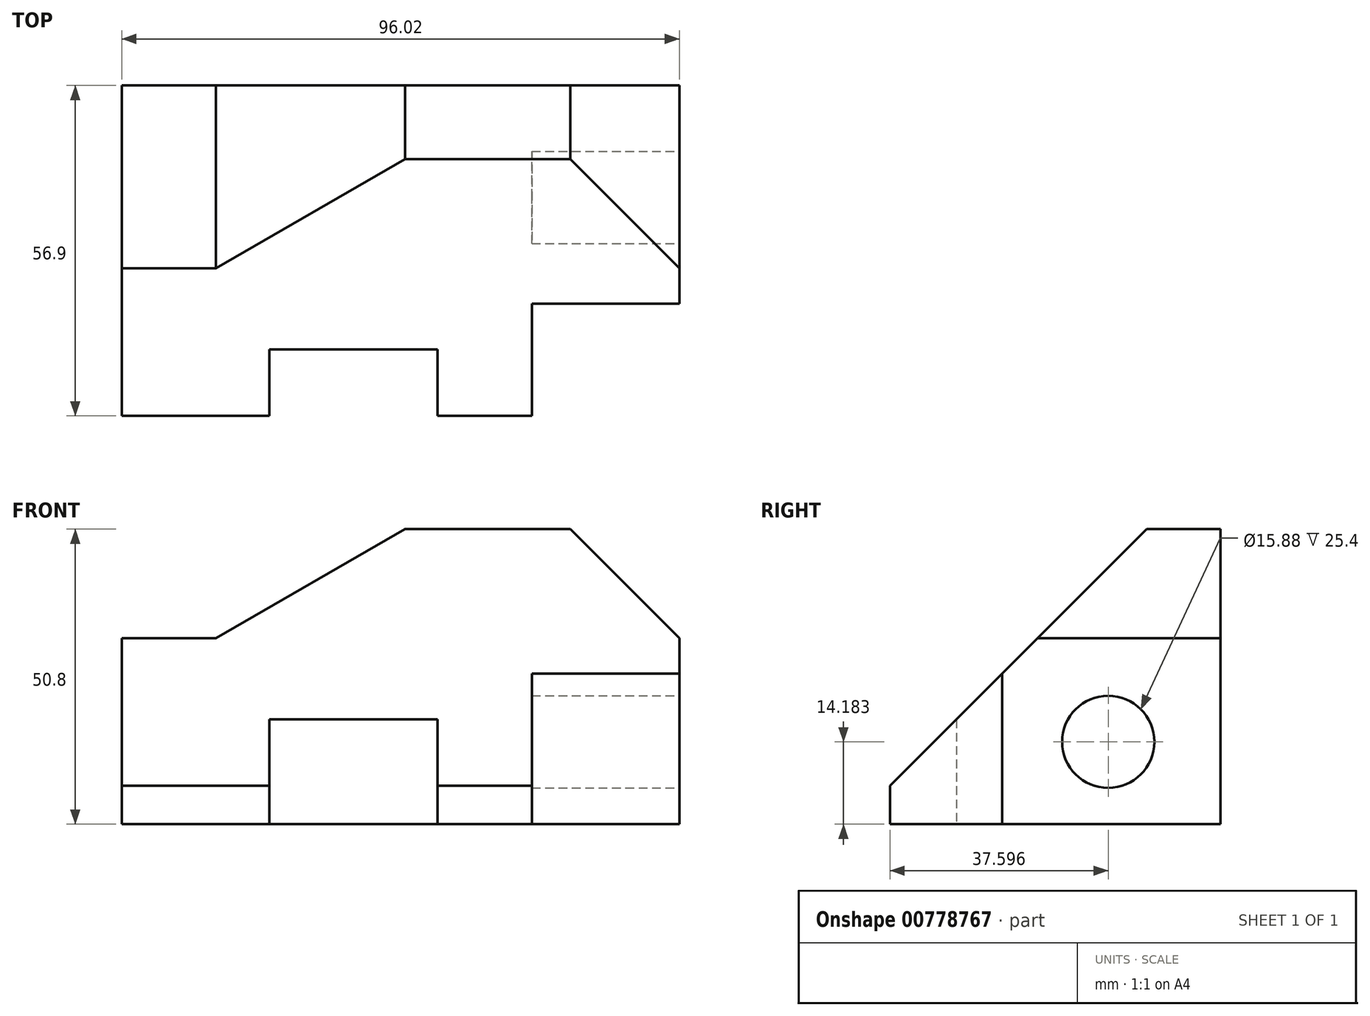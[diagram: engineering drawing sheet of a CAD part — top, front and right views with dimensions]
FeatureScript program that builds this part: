
annotation { "Feature Type Name" : "Feature", "Feature Type Description" : "" }
export const myFeature = defineFeature(function(context is Context, id is Id, definition is map)
    precondition{}
    {
        {
            var Q0;
            Q0=qCreatedBy(makeId("Top.planeOp"),FACE);
            var sketch = newSketch(context, id + "F0", { "sketchPlane" : qUnion([Q0])});
            skLineSegment(sketch, "E0.bottom", {"start": v(48, -28.45) * mm, "end": v(-48, -28.45) * mm});
            skLineSegment(sketch, "E0.top", {"start": v(48, 28.45) * mm, "end": v(-48, 28.45) * mm});
            skLineSegment(sketch, "E0.left", {"start": v(48, -28.45) * mm, "end": v(48, 28.45) * mm});
            skLineSegment(sketch, "E0.right", {"start": v(-48, -28.45) * mm, "end": v(-48, 28.45) * mm});
            skPoint(sketch, "E0.middle", {"position": v(0, 0) * mm});
            skSolve(sketch);
        }
        {
            var Q0;
            Q0=qSketchRegion(id+"F0",true);
            extrude(context, id + "F1", {"entities" : qUnion([Q0]), "depth" : 50.8 * mm, "offsetDistance" : 25.4 * mm});
        }
        {
            var Q0;
            Q0=makeQuery(id+"F1.opExtrude","SWEPT_FACE",FACE,{"disambiguationData":[OSD([sQuery(id+"F0.wireOp",EDGE,"E0.left")])]});
            var sketch = newSketch(context, id + "F2", { "sketchPlane" : qUnion([Q0])});
            skLineSegment(sketch, "E1", {"start": v(15.75, 50.8) * mm, "end": v(-28.45, 50.8) * mm});
            skLineSegment(sketch, "E2", {"start": v(-28.45, 50.8) * mm, "end": v(-28.45, 6.6) * mm});
            skLineSegment(sketch, "E3", {"start": v(-28.45, 6.6) * mm, "end": v(15.75, 50.8) * mm});
            skSolve(sketch);
        }
        {
            var Q0;
            Q0=makeQuery(id+"F2.imprint","IMPRINT",FACE,{"disambiguationData":[TD([[makeQuery(id+"F2.imprint","IMPRINT",EDGE,{"derivedFrom":sQuery(id+"F2.wireOp",EDGE,"E1")}),-1.0]])]});
            extrude(context, id + "F3", {"entities" : qUnion([Q0]), "operationType" : NewBodyOperationType.REMOVE, "oppositeDirection" : true, "depth" : 96.01 * mm, "offsetDistance" : 25.4 * mm});
        }
        {
            var Q0;
            Q0=makeQuery(id+"F1.opExtrude","SWEPT_FACE",FACE,{"disambiguationData":[OSD([sQuery(id+"F0.wireOp",EDGE,"E0.top")])]});
            var sketch = newSketch(context, id + "F4", { "sketchPlane" : qUnion([Q0])});
            skLineSegment(sketch, "E4", {"start": v(-29.21, 50.8) * mm, "end": v(-48, 50.8) * mm});
            skLineSegment(sketch, "E5", {"start": v(-48, 50.8) * mm, "end": v(-48, 32) * mm});
            skLineSegment(sketch, "E6", {"start": v(-48, 32) * mm, "end": v(-29.21, 50.8) * mm});
            skSolve(sketch);
        }
        {
            var Q0;
            Q0=makeQuery(id+"F4.imprint","IMPRINT",FACE,{"disambiguationData":[TD([[makeQuery(id+"F4.imprint","IMPRINT",EDGE,{"derivedFrom":sQuery(id+"F4.wireOp",EDGE,"E5")}),1.0]])]});
            extrude(context, id + "F5", {"entities" : qUnion([Q0]), "operationType" : NewBodyOperationType.REMOVE, "oppositeDirection" : true, "depth" : 31.75 * mm, "offsetDistance" : 25.4 * mm});
        }
        {
            var Q0;
            Q0=makeQuery(id+"F1.opExtrude","SWEPT_FACE",FACE,{"disambiguationData":[OSD([sQuery(id+"F0.wireOp",EDGE,"E0.left")])]});
            var sketch = newSketch(context, id + "F6", { "sketchPlane" : qUnion([Q0])});
            skLineSegment(sketch, "E7", {"start": v(-28.45, 6.6) * mm, "end": v(-28.45, 0) * mm});
            skLineSegment(sketch, "E8", {"start": v(-28.45, 0) * mm, "end": v(-9.14, 0) * mm});
            skLineSegment(sketch, "E9", {"start": v(-9.14, 0) * mm, "end": v(-9.14, 25.9) * mm});
            skLineSegment(sketch, "E10", {"start": v(-9.14, 25.9) * mm, "end": v(-28.45, 6.6) * mm});
            skSolve(sketch);
        }
        {
            var Q0;
            Q0=makeQuery(id+"F6.imprint","IMPRINT",FACE,{"disambiguationData":[TD([[makeQuery(id+"F6.imprint","IMPRINT",EDGE,{"derivedFrom":sQuery(id+"F6.wireOp",EDGE,"E7")}),1.0]])]});
            extrude(context, id + "F7", {"entities" : qUnion([Q0]), "operationType" : NewBodyOperationType.REMOVE, "oppositeDirection" : true, "depth" : 25.4 * mm, "offsetDistance" : 25.4 * mm});
        }
        {
            var Q0;
            Q0=makeQuery(id+"F1.opExtrude","CAP_FACE",FACE,{"disambiguationData":[OSD([sQuery(id+"F0.wireOp",EDGE,"E0.bottom"),sQuery(id+"F0.wireOp",EDGE,"E0.top"),sQuery(id+"F0.wireOp",EDGE,"E0.left"),sQuery(id+"F0.wireOp",EDGE,"E0.right")])],"isStart":true});
            var sketch = newSketch(context, id + "F8", { "sketchPlane" : qUnion([Q0])});
            skLineSegment(sketch, "E11", {"start": v(-48, 28.45) * mm, "end": v(-22.6, 28.45) * mm});
            skLineSegment(sketch, "E12", {"start": v(-22.6, 28.45) * mm, "end": v(-22.6, 17.02) * mm});
            skLineSegment(sketch, "E13", {"start": v(-22.6, 17.02) * mm, "end": v(6.35, 17.02) * mm});
            skLineSegment(sketch, "E14", {"start": v(6.35, 17.02) * mm, "end": v(6.35, 28.45) * mm});
            skLineSegment(sketch, "E15", {"start": v(6.35, 28.45) * mm, "end": v(-22.6, 28.45) * mm});
            skSolve(sketch);
        }
        {
            var Q0;
            Q0=makeQuery(id+"F8.imprint","IMPRINT",FACE,{"disambiguationData":[TD([[makeQuery(id+"F8.imprint","IMPRINT",EDGE,{"derivedFrom":sQuery(id+"F8.wireOp",EDGE,"E12")}),1.0]])]});
            extrude(context, id + "F9", {"entities" : qUnion([Q0]), "operationType" : NewBodyOperationType.REMOVE, "oppositeDirection" : true, "depth" : 59.44 * mm, "offsetDistance" : 25.4 * mm});
        }
        {
            var Q0;
            Q0=makeQuery(id+"F1.opExtrude","SWEPT_FACE",FACE,{"disambiguationData":[OSD([sQuery(id+"F0.wireOp",EDGE,"E0.top")])]});
            var sketch = newSketch(context, id + "F10", { "sketchPlane" : qUnion([Q0])});
            skLineSegment(sketch, "E16", {"start": v(-29.21, 50.8) * mm, "end": v(-0.76, 50.8) * mm});
            skLineSegment(sketch, "E17", {"start": v(-0.76, 50.8) * mm, "end": v(48, 50.8) * mm});
            skLineSegment(sketch, "E18", {"start": v(48, 50.8) * mm, "end": v(48, 32) * mm});
            skLineSegment(sketch, "E19", {"start": v(-0.76, 50.8) * mm, "end": v(31.8, 32) * mm});
            skLineSegment(sketch, "E20", {"start": v(31.8, 32) * mm, "end": v(48, 32) * mm});
            skSolve(sketch);
        }
        {
            var Q0;
            Q0=makeQuery(id+"F10.imprint","IMPRINT",FACE,{"disambiguationData":[TD([[makeQuery(id+"F10.imprint","IMPRINT",EDGE,{"derivedFrom":sQuery(id+"F10.wireOp",EDGE,"E17")}),-1.0]])]});
            extrude(context, id + "F11", {"entities" : qUnion([Q0]), "operationType" : NewBodyOperationType.REMOVE, "oppositeDirection" : true, "depth" : 37.08 * mm, "offsetDistance" : 25.4 * mm});
        }
        {
            var Q0;
            Q0=makeQuery(id+"F1.opExtrude","SWEPT_FACE",FACE,{"disambiguationData":[OSD([sQuery(id+"F0.wireOp",EDGE,"E0.left")])]});
            var sketch = newSketch(context, id + "F12", { "sketchPlane" : qUnion([Q0])});
            skCircle(sketch, "E21", {"center": v(9.15, 14.18) * mm, "radius": 7.94 * mm});
            skSolve(sketch);
        }
        {
            var Q0;
            Q0=makeQuery(id+"F12.imprint","IMPRINT",FACE,{"disambiguationData":[TD([[makeQuery(id+"F12.imprint","IMPRINT",EDGE,{"derivedFrom":sQuery(id+"F12.wireOp",EDGE,"E21")}),1.0]])]});
            extrude(context, id + "F13", {"entities" : qUnion([Q0]), "operationType" : NewBodyOperationType.REMOVE, "oppositeDirection" : true, "depth" : 25.4 * mm, "offsetDistance" : 25.4 * mm});
        }
    });
